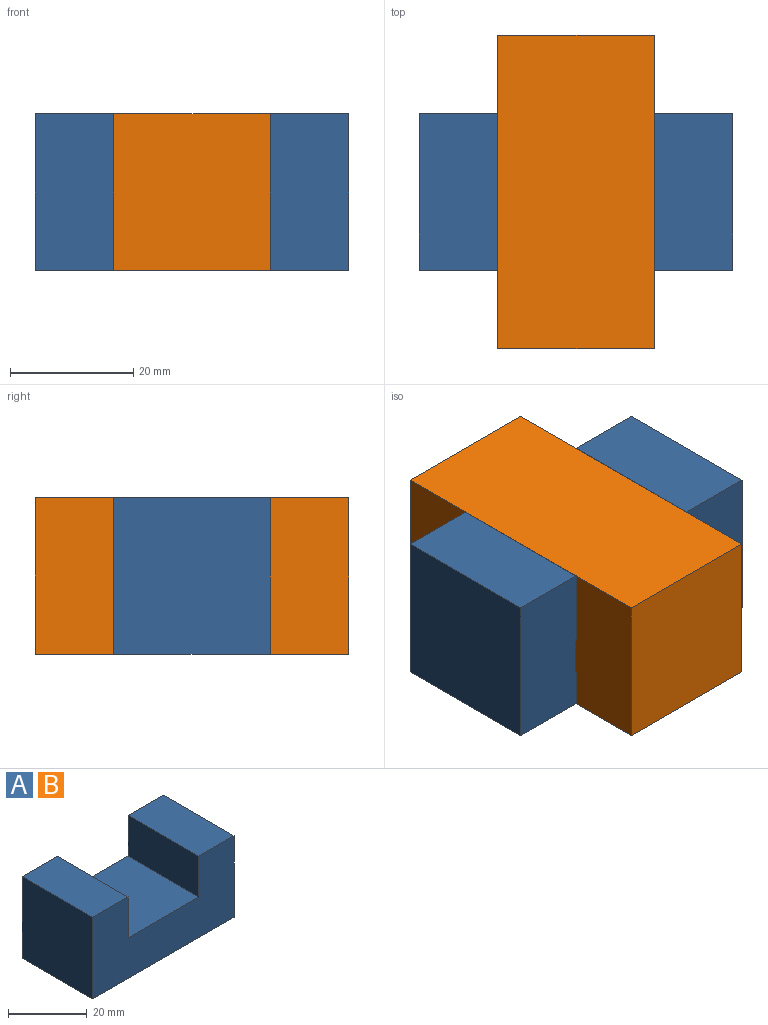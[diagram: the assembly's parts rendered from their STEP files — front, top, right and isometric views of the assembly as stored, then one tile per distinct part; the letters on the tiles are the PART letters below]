
ASSEMBLY  parts=2 mates=1
PART A: 10 faces, bbox 50.8x25.4x25.4 mm
  f0: plane 25.4x12.7mm, normal (0,0,1), area 322.6mm2, adj f1,f7,f8,f9
  f1: plane 25.4x25.4mm, normal (-1,0,0), area 645.2mm2, adj f0,f2,f8,f9
  f2: plane 50.8x25.4mm, normal (0,0,-1), area 1290.3mm2, adj f1,f3,f8,f9
  f3: plane 25.4x25.4mm, normal (1,0,0), area 645.2mm2, adj f2,f4,f8,f9
  f4: plane 25.4x12.7mm, normal (0,0,1), area 322.6mm2, adj f3,f5,f8,f9
  f5: plane 25.4x12.7mm, normal (-1,0,0), area 322.6mm2, adj f4,f6,f8,f9
  f6: plane 25.4x25.4mm, normal (0,0,1), area 645.2mm2, adj f5,f7,f8,f9
  f7: plane 25.4x12.7mm, normal (1,0,0), area 322.6mm2, adj f0,f6,f8,f9
  f8: plane 50.8x25.4mm, normal (0,-1,0), area 967.7mm2, adj f0,f1,f2,f3,f4,f5,f6,f7
  f9: plane 50.8x25.4mm, normal (0,1,0), area 967.7mm2, adj f0,f1,f2,f3,f4,f5,f6,f7
PART B: same geometry as A
PLACE A t=(-18.09,-2.57,-0.89)mm
PLACE B rot(axis=(0.71,-0.71,0),180deg) t=(-18.09,-2.57,24.51)mm
MATE fastened B.f4 <-> A.f2  axis (0,0,-1) through (-18.09,-15.27,-0.89)mm
